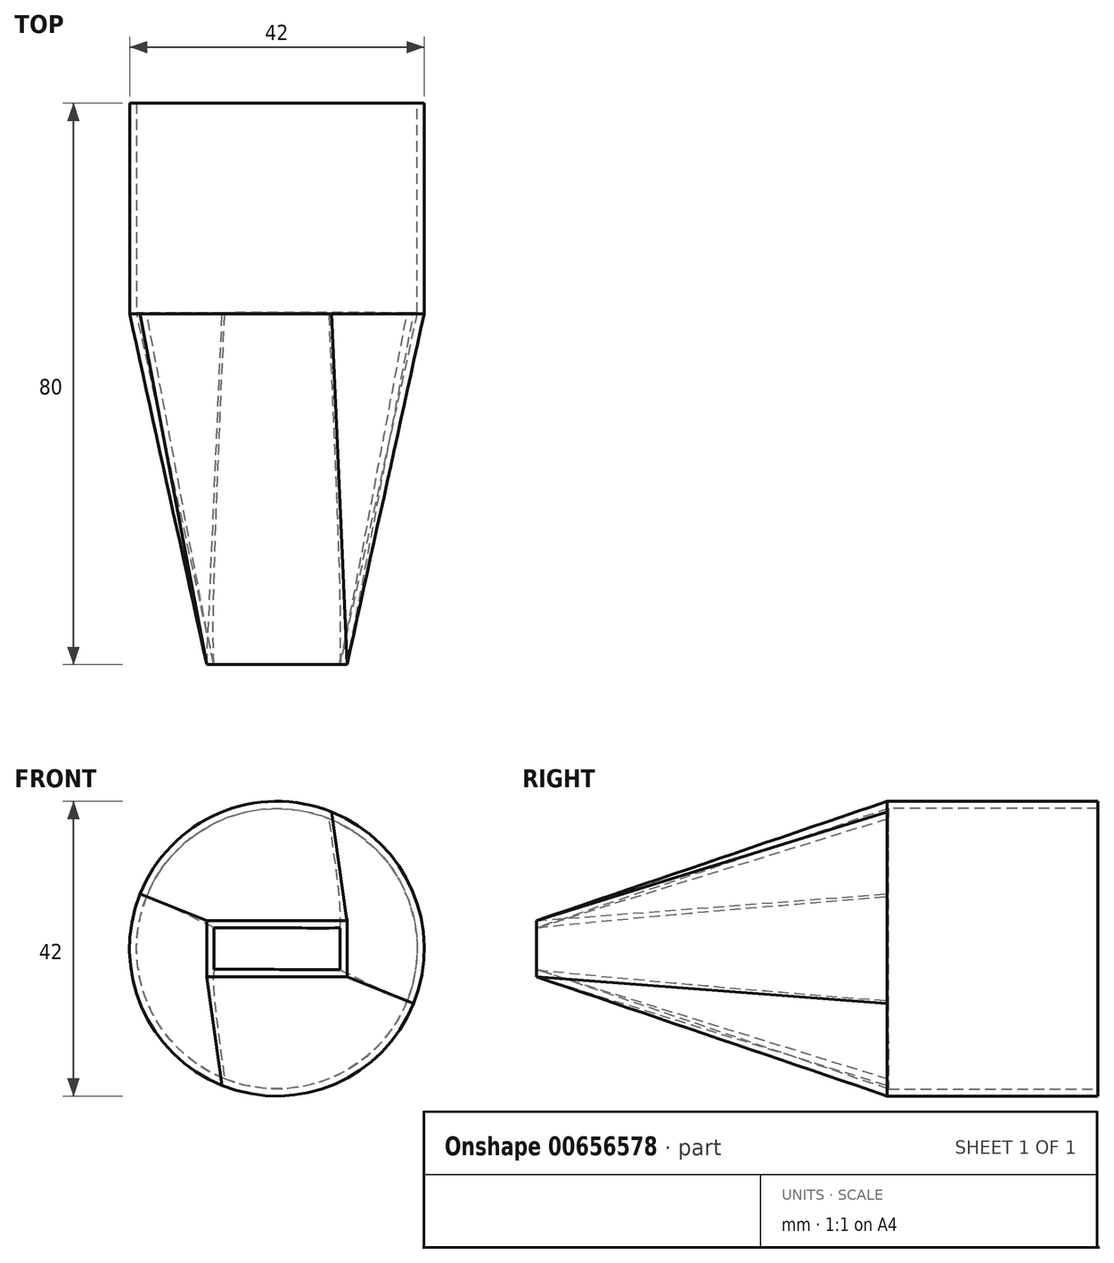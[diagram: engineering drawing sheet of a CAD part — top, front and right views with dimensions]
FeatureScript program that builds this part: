
annotation { "Feature Type Name" : "Feature", "Feature Type Description" : "" }
export const myFeature = defineFeature(function(context is Context, id is Id, definition is map)
    precondition{}
    {
        {
            var Q0;
            Q0=qCreatedBy(makeId("Front.planeOp"),FACE);
            var sketch = newSketch(context, id + "F0", { "sketchPlane" : qUnion([Q0])});
            skCircle(sketch, "E0", {"center": v(0, 0) * mm, "radius": 21 * mm});
            skSolve(sketch);
        }
        {
            var Q0;
            Q0=qCreatedBy(makeId("Front.planeOp"),FACE);
            cPlane(context, id + "F1", {"entities" : qUnion([Q0]), "cplaneType" : CPlaneType.OFFSET, "offset" : 50 * mm, "width" : 150 * mm, "height" : 150 * mm});
        }
        {
            var Q0;
            Q0=qCreatedBy(id+"F1.planeOp",FACE);
            var sketch = newSketch(context, id + "F2", { "sketchPlane" : qUnion([Q0])});
            skLineSegment(sketch, "E1.bottom", {"start": v(-10, 4) * mm, "end": v(10, 4) * mm});
            skLineSegment(sketch, "E1.top", {"start": v(-10, -4) * mm, "end": v(10, -4) * mm});
            skLineSegment(sketch, "E1.left", {"start": v(-10, 4) * mm, "end": v(-10, -4) * mm});
            skLineSegment(sketch, "E1.right", {"start": v(10, 4) * mm, "end": v(10, -4) * mm});
            skSolve(sketch);
        }
        {
            var Q0;
            Q0=makeQuery(id+"F2.imprint","IMPRINT",FACE,{"disambiguationData":[TD([[makeQuery(id+"F2.imprint","IMPRINT",EDGE,{"derivedFrom":sQuery(id+"F2.wireOp",EDGE,"E1.bottom")}),-1.0]])]});
            var Q1;
            Q1=makeQuery(id+"F0.imprint","IMPRINT",FACE,{"disambiguationData":[TD([[makeQuery(id+"F0.imprint","IMPRINT",EDGE,{"derivedFrom":sQuery(id+"F0.wireOp",EDGE,"E0")}),1.0]])]});
            loft(context, id + "F3", {"sheetProfilesArray" : [{ "sheetProfileEntities" : qUnion([Q0]) }, { "sheetProfileEntities" : qUnion([Q1]) }]});
        }
        {
            var Q0;
            Q0=qCreatedBy(makeId("Front.planeOp"),FACE);
            cPlane(context, id + "F4", {"entities" : qUnion([Q0]), "cplaneType" : CPlaneType.OFFSET, "offset" : 30 * mm, "oppositeDirection" : true, "width" : 150 * mm, "height" : 150 * mm});
        }
        {
            var Q0;
            Q0=qCreatedBy(id+"F4.planeOp",FACE);
            var sketch = newSketch(context, id + "F5", { "sketchPlane" : qUnion([Q0])});
            skCircle(sketch, "E2", {"center": v(0, 0) * mm, "radius": 21 * mm});
            skSolve(sketch);
        }
        {
            var Q1;
            Q1=makeQuery(id+"F3.opLoft","CAP_FACE",FACE,{"disambiguationData":[OSD([makeQuery(id+"F0.imprint","IMPRINT",FACE,{"disambiguationData":[TD([[makeQuery(id+"F0.imprint","IMPRINT",EDGE,{"derivedFrom":sQuery(id+"F0.wireOp",EDGE,"E0")}),1.0]])]})])],"isStart":true});
            var Q2;
            Q2=makeQuery(id+"F5.imprint","IMPRINT",FACE,{"disambiguationData":[TD([[makeQuery(id+"F5.imprint","IMPRINT",EDGE,{"derivedFrom":sQuery(id+"F5.wireOp",EDGE,"E2")}),1.0]])]});
            loft(context, id + "F6", {"operationType" : NewBodyOperationType.ADD, "sheetProfilesArray" : [{ "sheetProfileEntities" : qUnion([Q1]) }, { "sheetProfileEntities" : qUnion([Q2]) }]});
        }
        {
            var Q0;
            Q0=makeQuery(id+"F6.opLoft","CAP_FACE",FACE,{"disambiguationData":[OSD([makeQuery(id+"F5.imprint","IMPRINT",FACE,{"disambiguationData":[TD([[makeQuery(id+"F5.imprint","IMPRINT",EDGE,{"derivedFrom":sQuery(id+"F5.wireOp",EDGE,"E2")}),1.0]])]})])],"isStart":true});
            var Q1;
            Q1=makeQuery(id+"F3.opLoft","CAP_FACE",FACE,{"disambiguationData":[OSD([makeQuery(id+"F2.imprint","IMPRINT",FACE,{"disambiguationData":[TD([[makeQuery(id+"F2.imprint","IMPRINT",EDGE,{"derivedFrom":sQuery(id+"F2.wireOp",EDGE,"E1.bottom")}),-1.0]])]})])],"isStart":true});
            shell(context, id + "F7", {"entities" : qUnion([Q0, Q1]), "thickness" : 1 * mm});
        }
    });
